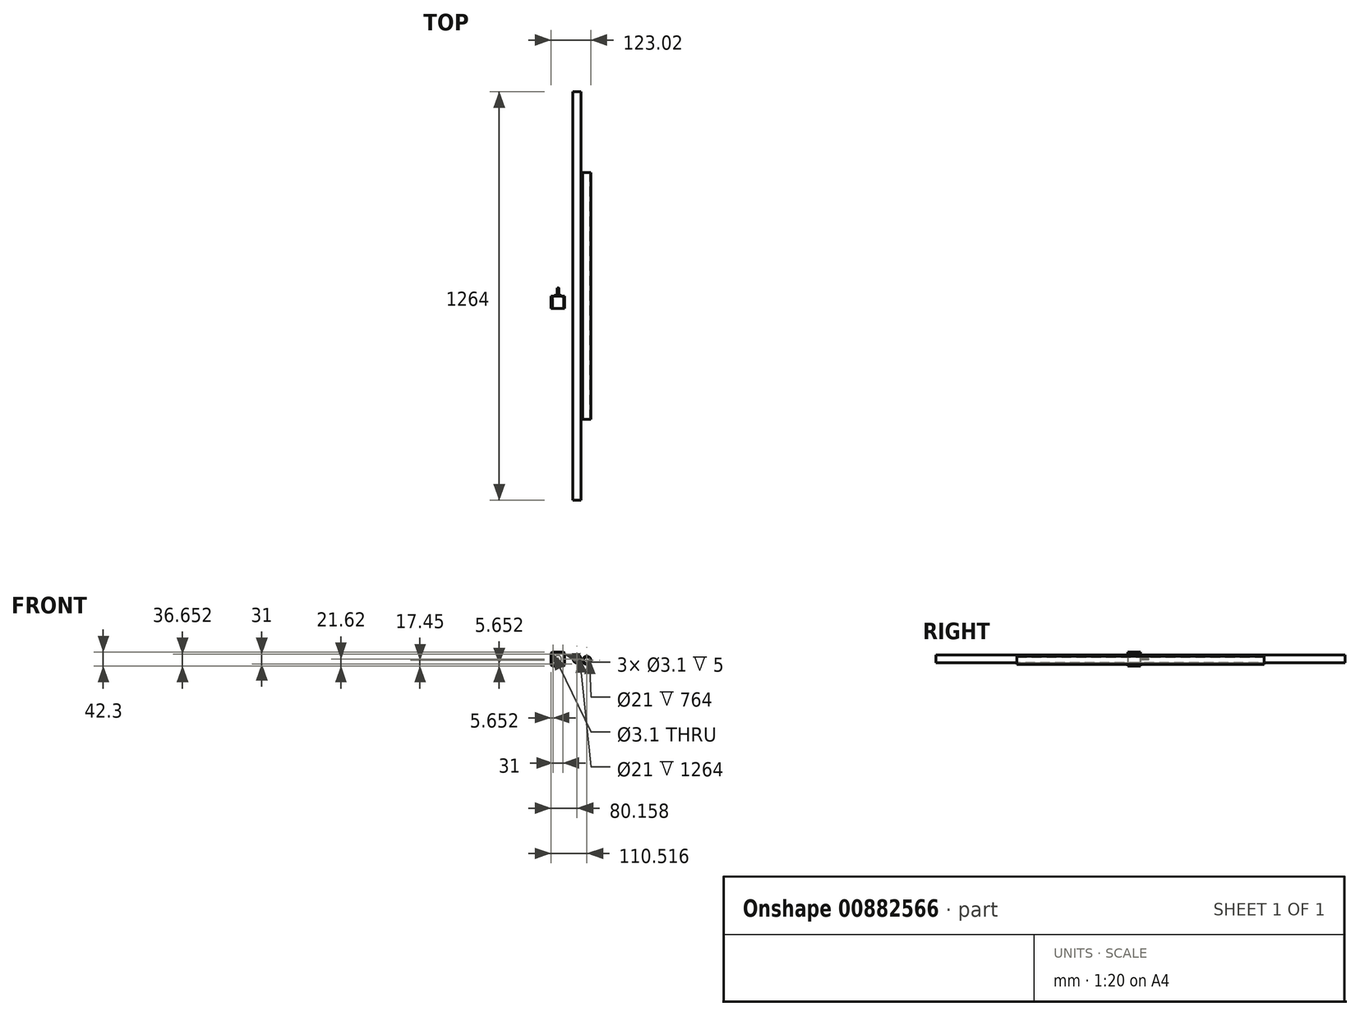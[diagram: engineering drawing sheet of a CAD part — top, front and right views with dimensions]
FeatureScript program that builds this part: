
annotation { "Feature Type Name" : "Feature", "Feature Type Description" : "" }
export const myFeature = defineFeature(function(context is Context, id is Id, definition is map)
    precondition{}
    {
        {
            var Q0;
            Q0=qCreatedBy(makeId("Front.planeOp"),FACE);
            var sketch = newSketch(context, id + "F0", { "sketchPlane" : qUnion([Q0])});
            skLineSegment(sketch, "E0.bottom", {"start": v(-49.25, 29.33) * mm, "end": v(-80.25, 29.33) * mm, "construction": true});
            skLineSegment(sketch, "E0.top", {"start": v(-49.25, -1.67) * mm, "end": v(-80.25, -1.67) * mm, "construction": true});
            skLineSegment(sketch, "E0.left", {"start": v(-49.25, 29.33) * mm, "end": v(-49.25, -1.67) * mm, "construction": true});
            skLineSegment(sketch, "E0.right", {"start": v(-80.25, 29.33) * mm, "end": v(-80.25, -1.67) * mm, "construction": true});
            skPoint(sketch, "E0.middle", {"position": v(-64.75, 13.83) * mm});
            skLineSegment(sketch, "E1.bottom", {"start": v(-43.6, 34.98) * mm, "end": v(-85.9, 34.98) * mm});
            skLineSegment(sketch, "E1.top", {"start": v(-43.6, -7.32) * mm, "end": v(-85.9, -7.32) * mm});
            skLineSegment(sketch, "E1.left", {"start": v(-43.6, 34.98) * mm, "end": v(-43.6, -7.32) * mm});
            skLineSegment(sketch, "E1.right", {"start": v(-85.9, 34.98) * mm, "end": v(-85.9, -7.32) * mm});
            skCircle(sketch, "E2", {"center": v(-80.25, 29.33) * mm, "radius": 1.55 * mm});
            skCircle(sketch, "E3", {"center": v(-49.25, 29.33) * mm, "radius": 1.55 * mm});
            skCircle(sketch, "E4", {"center": v(-80.25, -1.67) * mm, "radius": 1.55 * mm});
            skCircle(sketch, "E5", {"center": v(-49.25, -1.67) * mm, "radius": 1.55 * mm});
            skCircle(sketch, "E6", {"center": v(-64.75, 13.83) * mm, "radius": 2.5 * mm});
            skCircle(sketch, "E7", {"center": v(-64.75, 13.83) * mm, "radius": 11 * mm});
            skSolve(sketch);
        }
        {
            var Q0;
            Q0=makeQuery(id+"F0.imprint","IMPRINT",FACE,{"disambiguationData":[TD([[makeQuery(id+"F0.imprint","IMPRINT",EDGE,{"derivedFrom":sQuery(id+"F0.wireOp",EDGE,"E1.bottom")}),1.0]])]});
            var Q1;
            Q1=makeQuery(id+"F0.imprint","IMPRINT",FACE,{"disambiguationData":[TD([[makeQuery(id+"F0.imprint","IMPRINT",EDGE,{"derivedFrom":sQuery(id+"F0.wireOp",EDGE,"E3")}),1.0]])]});
            var Q2;
            Q2=makeQuery(id+"F0.imprint","IMPRINT",FACE,{"disambiguationData":[TD([[makeQuery(id+"F0.imprint","IMPRINT",EDGE,{"derivedFrom":sQuery(id+"F0.wireOp",EDGE,"E5")}),1.0]])]});
            var Q3;
            Q3=makeQuery(id+"F0.imprint","IMPRINT",FACE,{"disambiguationData":[TD([[makeQuery(id+"F0.imprint","IMPRINT",EDGE,{"derivedFrom":sQuery(id+"F0.wireOp",EDGE,"E4")}),1.0]])]});
            var Q4;
            Q4=makeQuery(id+"F0.imprint","IMPRINT",FACE,{"disambiguationData":[TD([[makeQuery(id+"F0.imprint","IMPRINT",EDGE,{"derivedFrom":sQuery(id+"F0.wireOp",EDGE,"E2")}),-1.0]])]});
            var Q5;
            Q5=makeQuery(id+"F0.imprint","IMPRINT",FACE,{"disambiguationData":[TD([[makeQuery(id+"F0.imprint","IMPRINT",EDGE,{"derivedFrom":sQuery(id+"F0.wireOp",EDGE,"E6")}),-1.0]])]});
            var Q6;
            Q6=makeQuery(id+"F0.imprint","IMPRINT",FACE,{"disambiguationData":[TD([[makeQuery(id+"F0.imprint","IMPRINT",EDGE,{"derivedFrom":sQuery(id+"F0.wireOp",EDGE,"E6")}),1.0]])]});
            extrude(context, id + "F1", {"entities" : qUnion([Q0, Q1, Q2, Q3, Q4, Q5, Q6]), "depth" : 39 * mm, "offsetDistance" : 25 * mm});
        }
        {
            var Q0;
            Q0=makeQuery(id+"F1.opExtrude","SWEPT_EDGE",EDGE,{"disambiguationData":[OSD([sQuery(id+"F0.wireOp",EDGE,"E1.bottom"),sQuery(id+"F0.wireOp",EDGE,"E1.left")])]});
            var Q1;
            Q1=makeQuery(id+"F1.opExtrude","SWEPT_EDGE",EDGE,{"disambiguationData":[OSD([sQuery(id+"F0.wireOp",EDGE,"E1.bottom"),sQuery(id+"F0.wireOp",EDGE,"E1.right")])]});
            var Q2;
            Q2=makeQuery(id+"F1.opExtrude","SWEPT_EDGE",EDGE,{"disambiguationData":[OSD([sQuery(id+"F0.wireOp",EDGE,"E1.top"),sQuery(id+"F0.wireOp",EDGE,"E1.left")])]});
            var Q3;
            Q3=makeQuery(id+"F1.opExtrude","SWEPT_EDGE",EDGE,{"disambiguationData":[OSD([sQuery(id+"F0.wireOp",EDGE,"E1.top"),sQuery(id+"F0.wireOp",EDGE,"E1.right")])]});
            chamfer(context, id + "F2", {"entities" : qUnion([Q0, Q1, Q2, Q3]), "width" : 3 * mm, "tangentPropagation" : true});
        }
        {
            var Q0;
            Q0=makeQuery(id+"F0.imprint","IMPRINT",FACE,{"disambiguationData":[TD([[makeQuery(id+"F0.imprint","IMPRINT",EDGE,{"derivedFrom":sQuery(id+"F0.wireOp",EDGE,"E3")}),1.0]])]});
            var Q1;
            Q1=makeQuery(id+"F0.imprint","IMPRINT",FACE,{"disambiguationData":[TD([[makeQuery(id+"F0.imprint","IMPRINT",EDGE,{"derivedFrom":sQuery(id+"F0.wireOp",EDGE,"E2")}),-1.0]])]});
            var Q2;
            Q2=makeQuery(id+"F0.imprint","IMPRINT",FACE,{"disambiguationData":[TD([[makeQuery(id+"F0.imprint","IMPRINT",EDGE,{"derivedFrom":sQuery(id+"F0.wireOp",EDGE,"E4")}),1.0]])]});
            var Q3;
            Q3=makeQuery(id+"F0.imprint","IMPRINT",FACE,{"disambiguationData":[TD([[makeQuery(id+"F0.imprint","IMPRINT",EDGE,{"derivedFrom":sQuery(id+"F0.wireOp",EDGE,"E5")}),1.0]])]});
            extrude(context, id + "F3", {"entities" : qUnion([Q0, Q1, Q2, Q3]), "operationType" : NewBodyOperationType.REMOVE, "oppositeDirection" : true, "depth" : -5 * mm, "offsetDistance" : 25 * mm});
        }
        {
            var Q0;
            Q0=makeQuery(id+"F0.imprint","IMPRINT",FACE,{"disambiguationData":[TD([[makeQuery(id+"F0.imprint","IMPRINT",EDGE,{"derivedFrom":sQuery(id+"F0.wireOp",EDGE,"E6")}),1.0]])]});
            extrude(context, id + "F4", {"entities" : qUnion([Q0]), "operationType" : NewBodyOperationType.ADD, "depth" : -25 * mm, "offsetDistance" : 25 * mm});
        }
        {
            var Q0;
            Q0=qCreatedBy(makeId("Front.planeOp"),FACE);
            var sketch = newSketch(context, id + "F5", { "sketchPlane" : qUnion([Q0])});
            skCircle(sketch, "E8", {"center": v(-5.74, 14.3) * mm, "radius": 12.5 * mm});
            skCircle(sketch, "E9", {"center": v(-5.74, 14.3) * mm, "radius": 10.5 * mm});
            skSolve(sketch);
        }
        {
            var Q0;
            Q0=makeQuery(id+"F5.imprint","IMPRINT",FACE,{"disambiguationData":[TD([[makeQuery(id+"F5.imprint","IMPRINT",EDGE,{"derivedFrom":sQuery(id+"F5.wireOp",EDGE,"E8")}),1.0]])]});
            extrude(context, id + "F6", {"entities" : qUnion([Q0]), "endBound" : BoundingType.SYMMETRIC, "depth" : (1000 + 264) * mm, "offsetDistance" : 25 * mm});
        }
        {
            var Q0;
            Q0=qCreatedBy(makeId("Front.planeOp"),FACE);
            var sketch = newSketch(context, id + "F7", { "sketchPlane" : qUnion([Q0])});
            skCircle(sketch, "E10", {"center": v(24.62, 10.13) * mm, "radius": 12.5 * mm});
            skCircle(sketch, "E11", {"center": v(24.62, 10.13) * mm, "radius": 10.5 * mm});
            skSolve(sketch);
        }
        {
            var Q0;
            Q0=makeQuery(id+"F7.imprint","IMPRINT",FACE,{"disambiguationData":[TD([[makeQuery(id+"F7.imprint","IMPRINT",EDGE,{"derivedFrom":sQuery(id+"F7.wireOp",EDGE,"E10")}),1.0]])]});
            extrude(context, id + "F8", {"entities" : qUnion([Q0]), "endBound" : BoundingType.SYMMETRIC, "depth" : (500 + 264) * mm, "offsetDistance" : 25 * mm});
        }
        {
            var Q0;
            Q0=makeQuery(id+"F0.imprint","IMPRINT",FACE,{"disambiguationData":[TD([[makeQuery(id+"F0.imprint","IMPRINT",EDGE,{"derivedFrom":sQuery(id+"F0.wireOp",EDGE,"E6")}),-1.0]])]});
            extrude(context, id + "F9", {"entities" : qUnion([Q0]), "operationType" : NewBodyOperationType.ADD, "oppositeDirection" : true, "depth" : 2 * mm, "offsetDistance" : 25 * mm});
        }
    });
